# Revit family: Gleitlager T HV1, m.D., Ø20 - Ø60mm (h=100-126mm)
name_source: partatom
category: HLS-Bauteile
units: mm (PartAtom-declared; Revit-internal decimal feet)

## family parameters
Arbeitsebenenbasiert = Ja
Beim Laden mit Abzugskörper schneiden = Nein
Bemaßung runder Anschluss = Durchmesser verwenden
Beschriftungsausrichtung beibehalten = Nein
Gemeinsam genutzt = Ja
Immer vertikal = Nein
Klassifizierung = Keine
Raumberechnungspunkt = Nein
Teiletyp = Normal

## types (9) — shared parameters
Anzahl Rohrschellen = 2
Baustoffklasse = B2
Breite Schellenband = 35 mm
Breite Unterbau = 100 mm
Dämmstärke = 6 mm  [stored 0.019685 ft]
Fabrikat = MEFA
Hersteller = MEFA
Kurztext1 = Gleitlager T 2 RS HV1 35x4
Länge Unterbau = 250 mm
Material = Stahl
Materialname = S235
Mengeneinheit = St
Schalldämmeinlage = Gummi EPDM
Sicherheitsfaktor = 1.54
Stärke Material = 8 mm  [stored 0.0262467 ft]
Stärke Schellenband = 4 mm
Verschluss = Mutter / Verschluss-Schraube
Vorgabe-Ansicht = 1219 mm
max. Höhe Unterbau = 125 mm
max. Temperaturbeständigkeit = 100 °C
min. Höhe Unterbau = 100 mm
vpe = 1

## per-type parameters (varying)
| type | Artikelnummer | EAN | Gewicht | Gewicht pro Bauteil | Kurztext2 | Nennweite DN Rohr | Rohraußendurchmesser | Schellenteil | max. Rohrachse | max. Rohraußendurchmesser | min. Rohrachse | min. Rohraußendurchmesser |
| Gleitlager T HV1, m.2 RS, m.D., Ø 20-22 (h=100-126mm) | 141afbb0022 | 4250928460912 | 3.82 kg | 3.82 kg | 20 - 22 mm EPDM 100x250 mm fsv | 15 mm  [stored 0.0492126 ft] | 0 mm  [stored 0 ft] | TL-141S_b0030 bis 0068, m.D : mit RS Ø20-22mm m.D | 137 mm | 22 mm  [stored 0.0721785 ft] | 110 mm | 20 mm  [stored 0.0656168 ft] |
| Gleitlager T HV1, m.2 RS, m.D., Ø 25 (h=100-126mm) | 141afbb0025 | 4250928460929 | 3.86 kg | 3.86 kg | 25 mm EPDM 100x250 mm fsv | 0 mm  [stored 0 ft] | 25 mm  [stored 0.082021 ft] | TL-141S_b0030 bis 0068, m.D : mit RS Ø25mm m.D | 139 mm | 0 mm  [stored 0 ft] | 113 mm | 0 mm  [stored 0 ft] |
| Gleitlager T HV1, m.2 RS, m.D., Ø 27-28 (h=100-126mm) | 141afbb0028 | 4250928460936 | 3.89 kg | 3.89 kg | 27 - 28 mm EPDM 100x250 mm fsv | 20 mm  [stored 0.0656168 ft] | 0 mm  [stored 0 ft] | TL-141S_b0030 bis 0068, m.D : mit RS Ø27-28mm, m.D | 140 mm | 28 mm  [stored 0.0918635 ft] | 114 mm | 27 mm  [stored 0.0885827 ft] |
| Gleitlager T HV1, m.2 RS, m.D., Ø 32 (h=100-126mm) | 141afbb0032 | 4250928460943 | 3.93 kg | 3.93 kg | 32 mm EPDM 100x250 mm fsv | 0 mm  [stored 0 ft] | 32 mm  [stored 0.104987 ft] | TL-141S_b0030 bis 0068, m.D : mit RS Ø32mm m.D | 142 mm | 0 mm  [stored 0 ft] | 116 mm | 0 mm  [stored 0 ft] |
| Gleitlager T HV1, m.2 RS, m.D., Ø 33-35 (h=100-126mm) | 141afbb0035 | 4250928460950 | 3.96 kg | 3.96 kg | 33 - 35 mm EPDM 100x250 mm fsv | 25 mm  [stored 0.082021 ft] | 0 mm  [stored 0 ft] | TL-141S_b0030 bis 0068, m.D : mit RS Ø33-35mm m.D | 144 mm | 35 mm  [stored 0.114829 ft] | 117 mm | 33 mm  [stored 0.108268 ft] |
| Gleitlager T HV1, m.2 RS, m.D., Ø 40-42 (h=100-126mm) | 141afbb0042 | 4250928460967 | 4.02 kg | 4.02 kg | 37 - 42 mm EPDM 100x250 mm fsv | 32 mm  [stored 0.104987 ft] | 0 mm  [stored 0 ft] | TL-141S_b0030 bis 0068, m.D : mit RS Ø40-42mm m.D | 147 mm | 42 mm  [stored 0.137795 ft] | 120 mm | 37 mm  [stored 0.121391 ft] |
| Gleitlager T HV1, m.2 RS, m.D., Ø 48-50 (h=100-126mm) | 141afbb0050 | 4250928460974 | 4.09 kg | 4.09 kg | 44 - 50 mm EPDM 100x250 mm fsv | 40 mm  [stored 0.131234 ft] | 0 mm  [stored 0 ft] | TL-141S_b0030 bis 0068, m.D : mit RS Ø48-50mm m.D | 151 mm | 50 mm  [stored 0.164042 ft] | 124 mm | 44 mm  [stored 0.144357 ft] |
| Gleitlager T HV1, m.2 RS, m.D., Ø 54 (h=100-126mm) | 141afbb0054 | 4250928460981 | 4.13 kg | 4.13 kg | 54 mm EPDM 100x250 mm fsv | 0 mm  [stored 0 ft] | 54 mm  [stored 0.177165 ft] | TL-141S_b0030 bis 0068, m.D : mit RS Ø54mm m.D | 153 mm | 0 mm  [stored 0 ft] | 127 mm | 0 mm  [stored 0 ft] |
| Gleitlager T HV1, m.2 RS, m.D., Ø 60 (h=100-126mm) | 141afbb0060 | 4250928460998 | 4.19 kg | 4.19 kg | 60 mm EPDM 100x250 mm fsv | 50 mm  [stored 0.164042 ft] | 60 mm  [stored 0.19685 ft] | TL-141S_b0030 bis 0068, m.D : mit RS Ø60mm m.D | 156 mm | 0 mm  [stored 0 ft] | 130 mm | 0 mm  [stored 0 ft] |

note: [stored X ft] marks values corroborated as IEEE doubles in the binary element streams (Revit-internal decimal feet)

## geometry (parser evidence)
native form markers: Sweep x9
no freeform markers — native parametric forms only
